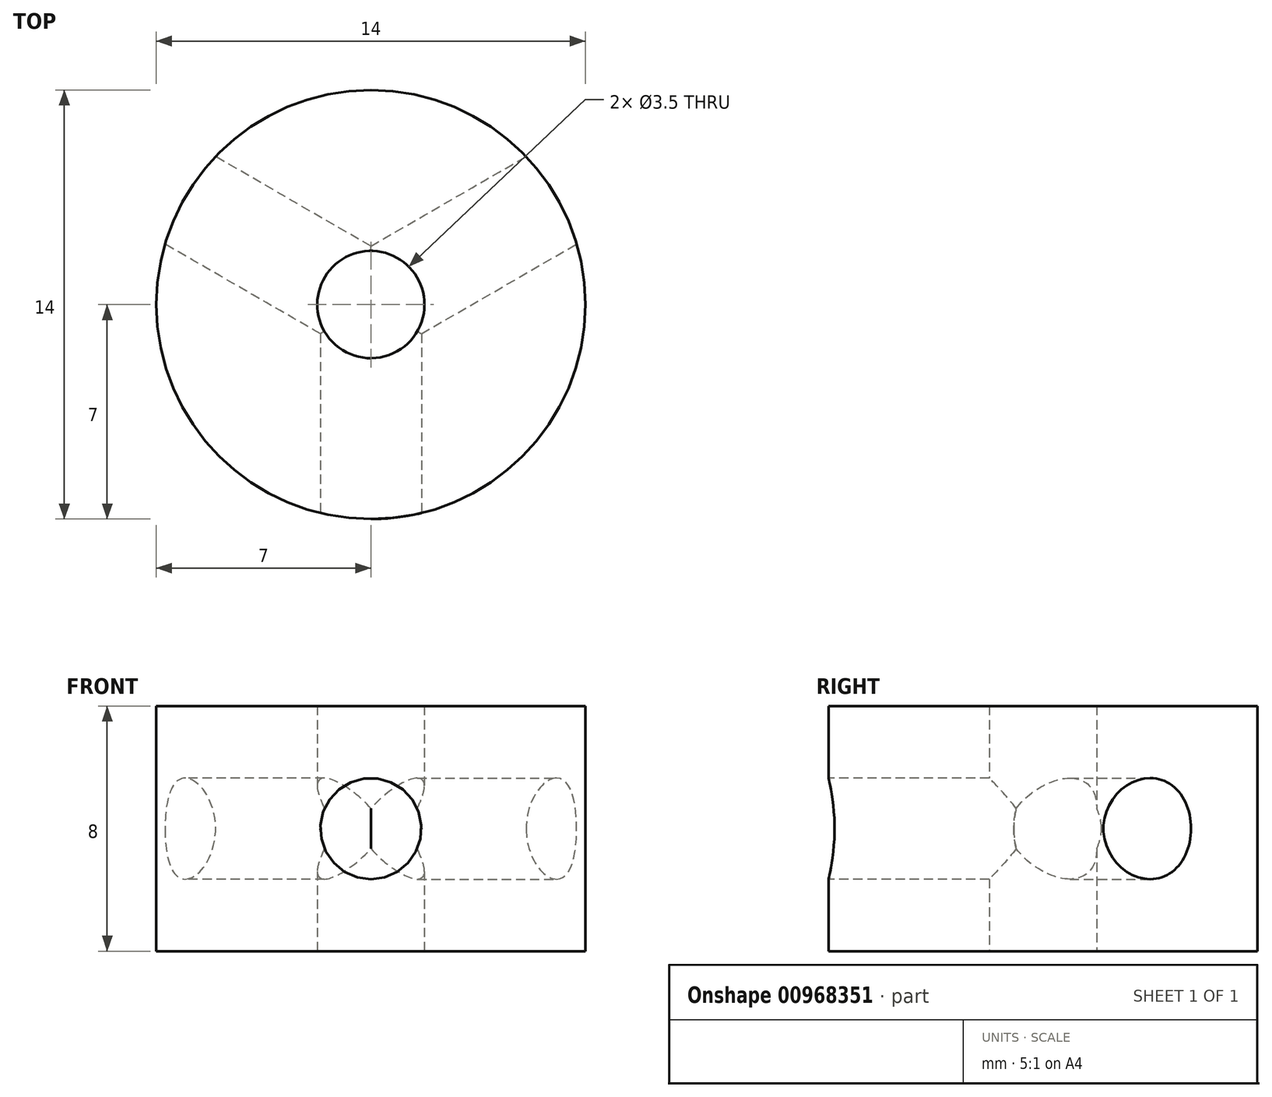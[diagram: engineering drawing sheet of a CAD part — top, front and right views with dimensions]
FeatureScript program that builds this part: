
annotation { "Feature Type Name" : "Feature", "Feature Type Description" : "" }
export const myFeature = defineFeature(function(context is Context, id is Id, definition is map)
    precondition{}
    {
        {
            var Q0;
            Q0=qCreatedBy(makeId("Top.planeOp"),FACE);
            var sketch = newSketch(context, id + "F0", { "sketchPlane" : qUnion([Q0])});
            skCircle(sketch, "E0", {"center": v(0, 0) * mm, "radius": 1.75 * mm});
            skCircle(sketch, "E1", {"center": v(0, 0) * mm, "radius": 7 * mm});
            skSolve(sketch);
        }
        {
            var Q0;
            Q0 = qSketchRegion(id + "F0", true);
            extrude(context, id + "F1", {"entities" : qUnion([Q0]), "endBound" : BoundingType.SYMMETRIC, "depth" : 8 * mm, "offsetDistance" : 25 * mm});
        }
        {
            var Q0;
            Q0=qCreatedBy(makeId("Front.planeOp"),FACE);
            var sketch = newSketch(context, id + "F2", { "sketchPlane" : qUnion([Q0])});
            skCircle(sketch, "E2", {"center": v(0, 0) * mm, "radius": 1.65 * mm});
            skSolve(sketch);
        }
        {
            var Q0;
            Q0 = qSketchRegion(id + "F2", true);
            extrude(context, id + "F3", {"entities" : qUnion([Q0]), "depth" : 7 * mm, "offsetDistance" : 25 * mm});
        }
        {
            var Q0;
            Q0=makeQuery(id+"F3.opExtrude","SWEPT_BODY",BODY,{"disambiguationData":[OSD([sQuery(id+"F2.wireOp",EDGE,"E2")])]});
            var Q1;
            Q1=makeQuery(id+"F1.opExtrude","CAP_EDGE",EDGE,{"disambiguationData":[OSD([sQuery(id+"F0.wireOp",EDGE,"E1")])],"isStart":false});
            circularPattern(context, id + "F4", {"entities" : qUnion([Q0]), "axis" : qUnion([Q1]), "angle" : 360 * degree, "instanceCount" : 3, "equalSpace" : true});
        }
        {
            var Q0;
            Q0=makeQuery(id+"F3.opExtrude","CAP_FACE",FACE,{"disambiguationData":[OSD([sQuery(id+"F2.wireOp",EDGE,"E2")])],"isStart":false});
            extrude(context, id + "F5", {"entities" : qUnion([Q0]), "operationType" : NewBodyOperationType.REMOVE, "oppositeDirection" : true, "depth" : 7 * mm, "offsetDistance" : 25 * mm});
        }
        {
            var Q0;
            Q0=makeQuery(id+"F4.opPattern","COPY",FACE,{"derivedFrom":makeQuery(id+"F3.opExtrude","CAP_FACE",FACE,{"disambiguationData":[OSD([sQuery(id+"F2.wireOp",EDGE,"E2")])],"isStart":false}),"instanceName":"1"});
            extrude(context, id + "F6", {"entities" : qUnion([Q0]), "operationType" : NewBodyOperationType.REMOVE, "oppositeDirection" : true, "depth" : 7 * mm, "offsetDistance" : 25 * mm});
        }
        {
            var Q0;
            Q0=makeQuery(id+"F4.opPattern","COPY",FACE,{"derivedFrom":makeQuery(id+"F3.opExtrude","CAP_FACE",FACE,{"disambiguationData":[OSD([sQuery(id+"F2.wireOp",EDGE,"E2")])],"isStart":false}),"instanceName":"2"});
            extrude(context, id + "F7", {"entities" : qUnion([Q0]), "operationType" : NewBodyOperationType.REMOVE, "oppositeDirection" : true, "depth" : 7 * mm, "offsetDistance" : 25 * mm});
        }
    });
